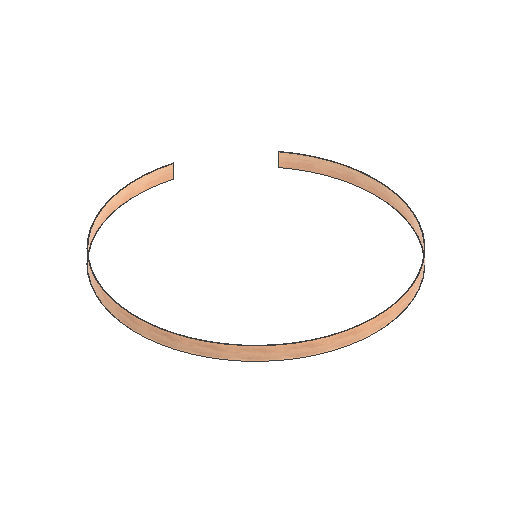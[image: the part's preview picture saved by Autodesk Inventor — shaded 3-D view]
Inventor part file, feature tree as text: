
AUTODESK INVENTOR PART (.ipt)
format: ipt  version: 2021 (Build 250183000, 183)  size: 124,416 bytes
history: native  units: mm
features: other x4, extrude x2, sketch x2, reference x2
ambient origin geometry x8: Origin, YZ Plane, XZ Plane, XY Plane, X Axis, Y Axis, Z Axis, Center Point
bodies: Solid1 (feature_tree)
feature tree (10):
  extrude  "Extrusion1"  Depth=100.0mm
  extrude  "Extrusion2"  Depth=100.0mm TaperAngle=0.0deg
  sketch  "Sketch1"  dims[d2=100.0mm d3=0.0mm d8=1761.52mm]
  sketch  "Sketch2"  dims[d9=1753.52mm d10=100.0mm d11=0.0mm]
  reference  "Reference1"
  reference  "Reference2"
  other  "Full Scale Assembly.iam"
  other  "Disc E Assembly:1"
  other  "Platform E4:1"
  other  "Platform E1:1"
